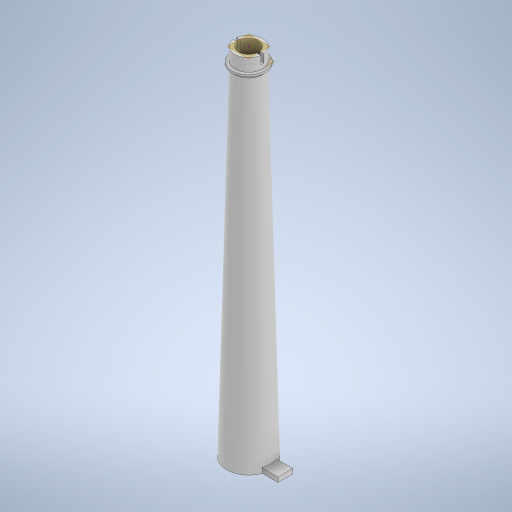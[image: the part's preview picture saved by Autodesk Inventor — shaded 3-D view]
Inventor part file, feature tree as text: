
AUTODESK INVENTOR PART (.ipt)
format: ipt  version: 2023 (Build 270158000, 158)  size: 338,432 bytes
history: native  units: in
note: dims shown in document units (in); Inventor stores cm internally (conversion verified against a paired STEP export)
features: sketch x13, extrude x6, plane x3, loft x2, chamfer x1, other x1
ambient origin geometry x8: Origin, YZ Plane, XZ Plane, XY Plane, X Axis, Y Axis, Z Axis, Center Point
bodies: Body1 (feature_tree)
feature tree (26):
  sketch  "Sketch11"  dims[d25=1.7717in d26=13.7795in d27=0.0in]
  sketch  "Sketch12"  dims[d28=0.0in d29=90.0deg d30=0.0in d31=90.0deg]
  extrude  "Extrusion3"  Depth=1.1024in
  loft  "Loft4"
  loft  "Loft5"
  plane  "Work Plane3"
  sketch  "Sketch18"  dims[d39=0.7874in d57=1.3386in]
  plane  "Work Plane4"
  plane  "Work Plane2"
  extrude  "Extrusion8"  TaperAngle=0.0deg  [1 undecoded]
  sketch  "Sketch21"  dims[d65=1.1024in d66=0.5118in d67=0.0in]
  chamfer  "Chamfer1"  Angle=90.0deg  [1 undecoded]
  extrude  "Extrusion9"  Depth=8.2677in
  extrude  "Extrusion10"  Depth=1.3386in
  extrude  "Extrusion11"  Depth=0.0787in TaperAngle=45.0deg
  extrude  "Extrusion12"  Depth=0.5118in TaperAngle=0.0deg
  sketch  "Sketch6"  dims[d10=2.7559in d24=1.1024in]
  sketch  "Sketch24"  dims[d70=0.3346in d71=0.0in]
  other  "Edges3"
  sketch  "Sketch13"  dims[d32=0.7874in d33=0.0in d34=90.0deg d35=0.0in d36=90.0deg]
  sketch  "Sketch14"  dims[d37=8.2677in d38=8.2677in]
  sketch  "Sketch20"  dims[d58=0.0787in d59=0.0in d62=0.1162in d63=0.0787in d64=45.0deg]
  sketch  "Sketch22"  dims[d68=0.126in]
  sketch  "Sketch23"  dims[d69=1.1811in]
  sketch  "Sketch25"  dims[d72=0.1969in]
  sketch  "Sketch26"  dims[d73=0.5906in d74=0.6693in d75=0.0984in d76=0.0in d77=0.8858in d78=0.5906in d80=0.5906in d81=0.1969in d82=0.0in d83=0.5906in d84=0.7992in d85=0.2087in d86=0.0906in d87=0.0in d8=0.0197in d9=0.0344in d11=0.0344in d88=0.0197in d89=0.0344in]
note: 2 required parameter values undecoded (feature->parameter linkage not recoverable at this tier; creation-order binding heuristic only, values carry confidence <= 0.55)
